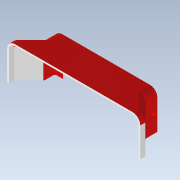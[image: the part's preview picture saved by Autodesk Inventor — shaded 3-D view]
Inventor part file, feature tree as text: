
AUTODESK INVENTOR PART (.ipt)
format: ipt  version: 2022.1 (Build 261234020, 234B)  size: 902,144 bytes
history: native  units: mm
features: extrude x1, sketch x1
ambient origin geometry x8: Origin, YZ Plane, XZ Plane, XY Plane, X Axis, Y Axis, Z Axis, Center Point
bodies: Volumenkörper2 (feature_tree), Volumenkörper1 (feature_tree)
feature tree (2):
  extrude  "Extrusion1"  Depth=1.0mm
  sketch  "Skizze1"  dims[d0=1.0mm d1=1.0mm d2=170.0mm d3=38.521424mm d4=38.521424mm d5=70.0mm d6=0.0mm d7=0.0mm]
